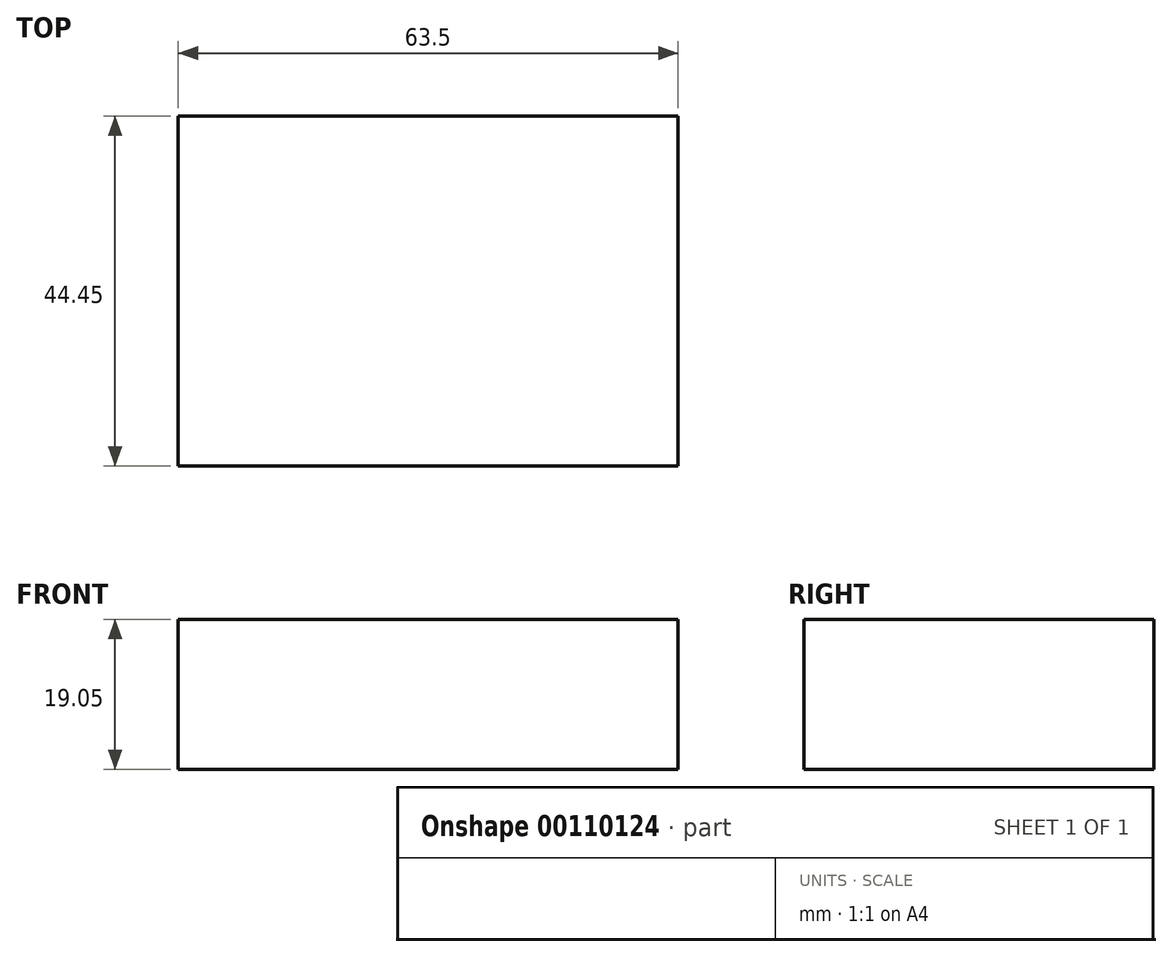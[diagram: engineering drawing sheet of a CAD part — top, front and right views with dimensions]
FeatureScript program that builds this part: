
annotation { "Feature Type Name" : "Feature", "Feature Type Description" : "" }
export const myFeature = defineFeature(function(context is Context, id is Id, definition is map)
    precondition{}
    {
        {
            var Q0;
            Q0=qCreatedBy(makeId("Front.planeOp"),FACE);
            var sketch = newSketch(context, id + "F0", { "sketchPlane" : qUnion([Q0])});
            skLineSegment(sketch, "E0.bottom", {"start": v(-10.6, 6.75) * mm, "end": v(52.9, 6.75) * mm});
            skLineSegment(sketch, "E0.top", {"start": v(-10.6, -12.3) * mm, "end": v(52.9, -12.3) * mm});
            skLineSegment(sketch, "E0.left", {"start": v(-10.6, 6.75) * mm, "end": v(-10.6, -12.3) * mm});
            skLineSegment(sketch, "E0.right", {"start": v(52.9, 6.75) * mm, "end": v(52.9, -12.3) * mm});
            skSolve(sketch);
        }
        {
            var Q0;
            Q0 = qSketchRegion(id + "F0", true);
            extrude(context, id + "F1", {"entities" : qUnion([Q0]), "depth" : 44.45 * mm});
        }
    });
